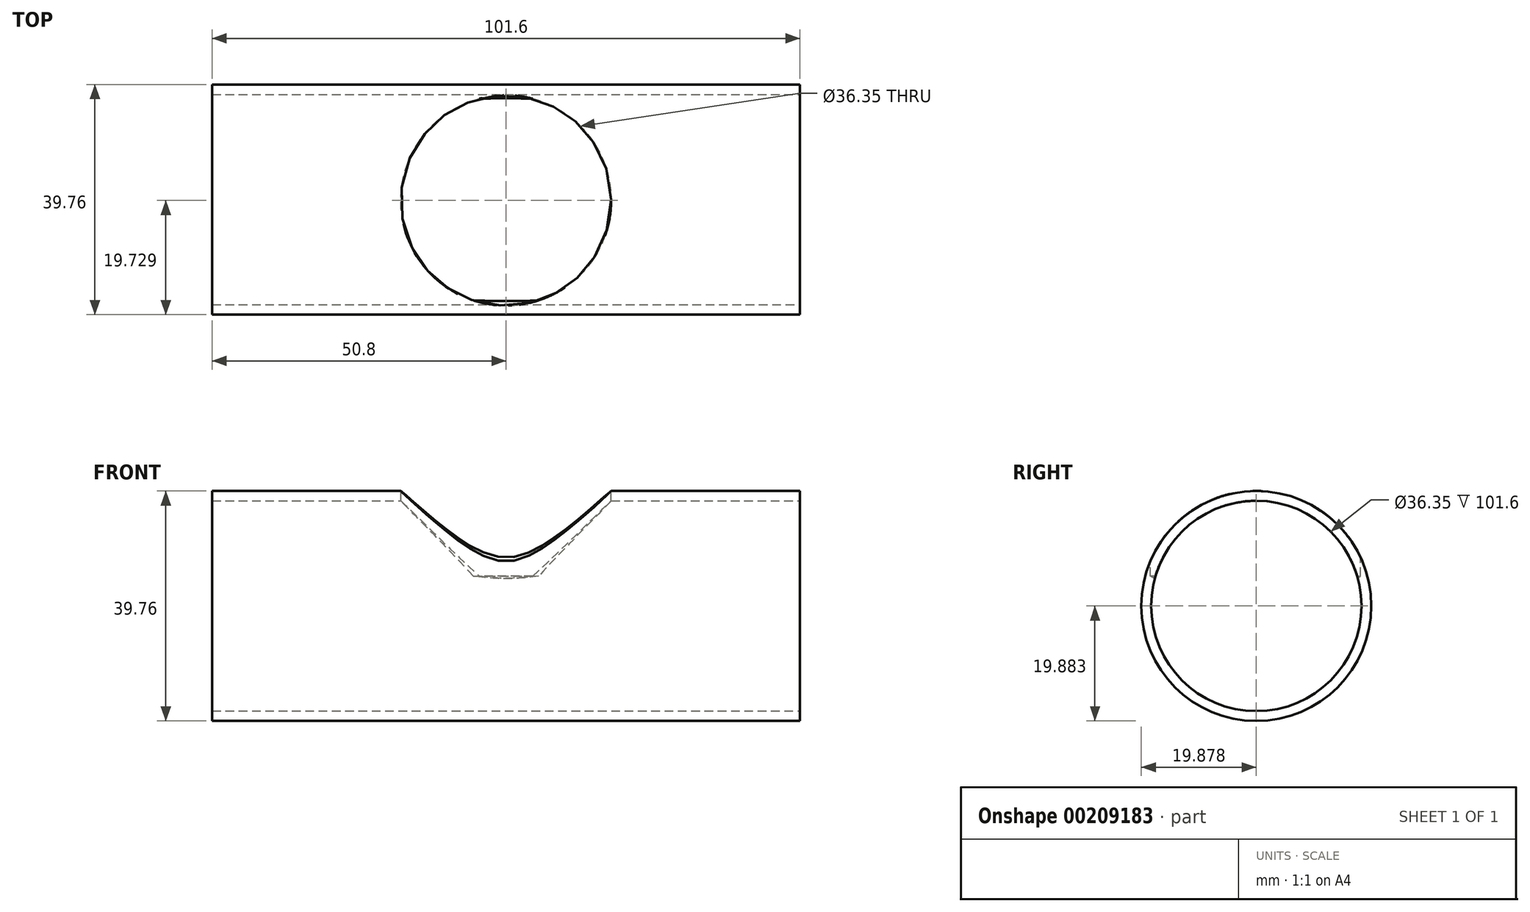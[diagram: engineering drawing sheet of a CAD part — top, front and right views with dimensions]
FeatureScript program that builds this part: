
annotation { "Feature Type Name" : "Feature", "Feature Type Description" : "" }
export const myFeature = defineFeature(function(context is Context, id is Id, definition is map)
    precondition{}
    {
        {
            var Q0;
            Q0=qCreatedBy(makeId("Right.planeOp"),FACE);
            var sketch = newSketch(context, id + "F0", { "sketchPlane" : qUnion([Q0])});
            skCircle(sketch, "E0", {"center": v(7.75, -46.34) * mm, "radius": 19.88 * mm});
            skSolve(sketch);
        }
        {
            var Q0;
            Q0=makeQuery(id+"F0.imprint","IMPRINT",FACE,{"disambiguationData":[TD([[makeQuery(id+"F0.imprint","IMPRINT",EDGE,{"derivedFrom":sQuery(id+"F0.wireOp",EDGE,"E0")}),1.0]])]});
            extrude(context, id + "F1", {"entities" : qUnion([Q0]), "endBound" : BoundingType.SYMMETRIC, "depth" : 101.6 * mm});
        }
        {
            var Q0;
            Q0=qCreatedBy(makeId("Top.planeOp"),FACE);
            var sketch = newSketch(context, id + "F2", { "sketchPlane" : qUnion([Q0])});
            skCircle(sketch, "E1", {"center": v(0, 7.6) * mm, "radius": 19.27 * mm});
            skSolve(sketch);
        }
        {
            var Q0;
            Q0=sQuery(id+"F2.wireOp",EDGE,"E1");
            extrude(context, id + "F3", {"bodyType" : ToolBodyType.SURFACE, "surfaceEntities" : qUnion([Q0]), "endBound" : BoundingType.UP_TO_NEXT, "oppositeDirection" : true, "depth" : 25.4 * mm});
        }
        {
            var Q0;
            Q0=qCreatedBy(makeId("Top.planeOp"),FACE);
            var sketch = newSketch(context, id + "F4", { "sketchPlane" : qUnion([Q0])});
            skCircle(sketch, "E2", {"center": v(0, 7.6) * mm, "radius": 19.27 * mm});
            skSolve(sketch);
        }
        {
            var Q0;
            Q0=sQuery(id+"F4.wireOp",VERTEX,"E2.center");
            var Q1;
            Q1=makeQuery(id+"F1.opExtrude","SWEPT_BODY",BODY,{"disambiguationData":[OSD([sQuery(id+"F0.wireOp",EDGE,"E0")])]});
            hole(context, id + "F5", {"style" : HoleStyle.SIMPLE, "endStyle" : HoleEndStyle.BLIND, "holeDiameter" : 38.1 * mm - 1.75 * mm, "holeDepth" : 2.54 * mm, "locations" : qUnion([Q0]), "scope" : qUnion([Q1])});
        }
        {
            var Q0;
            Q0=makeQuery(id+"F1.opExtrude","CAP_FACE",FACE,{"disambiguationData":[OSD([sQuery(id+"F0.wireOp",EDGE,"E0")])],"isStart":false});
            var Q1;
            Q1=makeQuery(id+"F1.opExtrude","CAP_FACE",FACE,{"disambiguationData":[OSD([sQuery(id+"F0.wireOp",EDGE,"E0")])],"isStart":true});
            shell(context, id + "F6", {"entities" : qUnion([Q0, Q1]), "thickness" : 1.75 * mm});
        }
        {
            var Q0;
            Q0=qCreatedBy(makeId("Right.planeOp"),FACE);
            var sketch = newSketch(context, id + "F7", { "sketchPlane" : qUnion([Q0])});
            skCircle(sketch, "E3", {"center": v(7.75, -46.34) * mm, "radius": 18.13 * mm});
            skSolve(sketch);
        }
        {
            var Q0;
            Q0=sQuery(id+"F7.wireOp",VERTEX,"E3.center");
            var Q1;
            Q1=makeQuery(id+"F1.opExtrude","SWEPT_BODY",BODY,{"disambiguationData":[OSD([sQuery(id+"F0.wireOp",EDGE,"E0")])]});
            hole(context, id + "F8", {"style" : HoleStyle.SIMPLE, "endStyle" : HoleEndStyle.THROUGH, "holeDiameter" : 38.1 * mm - 1.75 * mm, "locations" : qUnion([Q0]), "scope" : qUnion([Q1]), "isTappedThrough" : true});
        }
        {
            var Q0;
            Q0=sQuery(id+"F7.wireOp",VERTEX,"E3.center");
            var Q1;
            Q1=makeQuery(id+"F1.opExtrude","SWEPT_BODY",BODY,{"disambiguationData":[OSD([sQuery(id+"F0.wireOp",EDGE,"E0")])]});
            hole(context, id + "F9", {"style" : HoleStyle.SIMPLE, "endStyle" : HoleEndStyle.THROUGH, "oppositeDirection" : true, "holeDiameter" : 38.1 * mm - 1.75 * mm, "locations" : qUnion([Q0]), "scope" : qUnion([Q1]), "isTappedThrough" : true});
        }
    });
